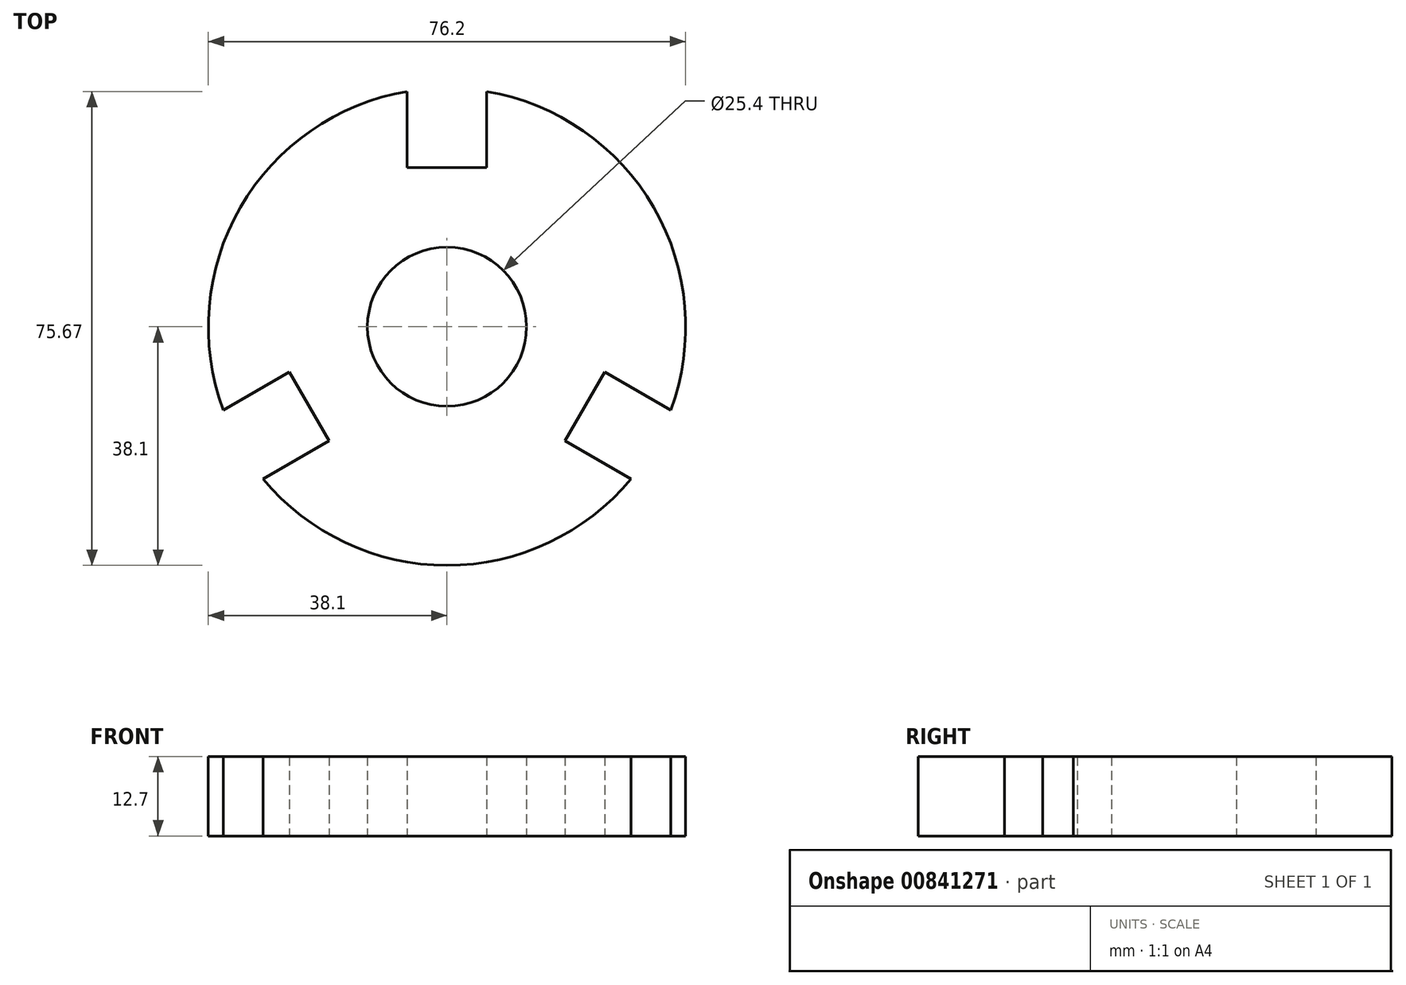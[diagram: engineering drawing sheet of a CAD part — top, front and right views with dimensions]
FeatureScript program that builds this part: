
annotation { "Feature Type Name" : "Feature", "Feature Type Description" : "" }
export const myFeature = defineFeature(function(context is Context, id is Id, definition is map)
    precondition{}
    {
        {
            var Q0;
            Q0=qCreatedBy(makeId("Top.planeOp"),FACE);
            var sketch = newSketch(context, id + "F0", { "sketchPlane" : qUnion([Q0])});
            skCircle(sketch, "E0", {"center": v(0, 0) * mm, "radius": 12.7 * mm});
            skArc(sketch, "E1.0", {"start": v(-6.35, 37.57) * mm, "mid": v(-33, 19.05) * mm, "end": v(-35.7, -13.28) * mm});
            skLineSegment(sketch, "E2", {"start": v(0, 0) * mm, "end": v(0, 59.91) * mm, "construction": true});
            skLineSegment(sketch, "E3", {"start": v(0, 0) * mm, "end": v(-54.47, -31.45) * mm, "construction": true});
            skLineSegment(sketch, "E4", {"start": v(0, 0) * mm, "end": v(56.73, -32.75) * mm, "construction": true});
            skPoint(sketch, "E5", {"position": v(0, 38.1) * mm});
            skPoint(sketch, "E6", {"position": v(-33, -19.05) * mm});
            skPoint(sketch, "E7", {"position": v(33, -19.05) * mm});
            skLineSegment(sketch, "E8.bottom", {"start": v(-6.35, 25.4) * mm, "end": v(6.35, 25.4) * mm});
            skLineSegment(sketch, "E8.left", {"start": v(-6.35, 25.4) * mm, "end": v(-6.35, 37.57) * mm});
            skLineSegment(sketch, "E8.right", {"start": v(6.35, 25.4) * mm, "end": v(6.35, 37.57) * mm});
            skPoint(sketch, "E9.orphan", {"position": v(6.35, 50.8) * mm});
            skPoint(sketch, "E8.top.start.orphan", {"position": v(-6.35, 50.8) * mm});
            skLineSegment(sketch, "E10.1.0", {"start": v(-18.82, -18.2) * mm, "end": v(-29.36, -24.28) * mm});
            skLineSegment(sketch, "E10.1.1", {"start": v(-18.82, -18.2) * mm, "end": v(-25.17, -7.2) * mm});
            skLineSegment(sketch, "E10.1.2", {"start": v(-25.17, -7.2) * mm, "end": v(-35.7, -13.28) * mm});
            skLineSegment(sketch, "E10.2.0", {"start": v(25.17, -7.2) * mm, "end": v(35.7, -13.28) * mm});
            skLineSegment(sketch, "E10.2.1", {"start": v(25.17, -7.2) * mm, "end": v(18.82, -18.2) * mm});
            skLineSegment(sketch, "E10.2.2", {"start": v(18.82, -18.2) * mm, "end": v(29.36, -24.28) * mm});
            skArc(sketch, "E11.trimOffspring", {"start": v(-29.36, -24.28) * mm, "mid": v(0, -38.1) * mm, "end": v(29.36, -24.28) * mm});
            skArc(sketch, "E12.trimOffspring", {"start": v(35.7, -13.28) * mm, "mid": v(33, 19.05) * mm, "end": v(6.35, 37.57) * mm});
            skSolve(sketch);
        }
        {
            var Q0;
            Q0 = qSketchRegion(id + "F0", true);
            extrude(context, id + "F1", {"entities" : qUnion([Q0]), "depth" : 12.7 * mm, "offsetDistance" : 25.4 * mm});
        }
    });
